# Revit family: Урна уличная круглая «Парко» Арт 12916
name_source: partatom
category: Антураж
revit_build: Autodesk Revit 2018 (Build: 20180423_1000(x64)
units: mm (PartAtom-declared; Revit-internal decimal feet)

## family parameters
Всегда вертикально = Да
Источник визуального образа = Геометрия семейства
На основе рабочей плоскости = Нет
Общий = Нет
При загрузке вырезать с полостями = Нет
Точка расчета площади = Нет

## types (2) — shared parameters
URL = https://hobbyka.ru
Артикул товара = Арт. 12916
Высота = 600 мм
Группа модели = Уличные урны
Диаметр = 388 мм
Длина = 388 мм
Изготовитель = ООО «Хоббика»
Изображение типоразмера = Урна уличная круглая «Парко» Арт 12916.jpg
Материал изделия = Сталь
Ширина = 388 мм

## per-type parameters (varying)
| type | Нержавеющая сталь | Описание | Сталь | Цвет урны |
| Версия "Сталь" | Нет | Урна уличная круглая «Парко». Версия сталь | Да | Сталь |
| Версия "Нержавеющая сталь" | Да | Урна уличная круглая «Парко». Версия нержавеющая сталь | Нет | Нержавеющая сталь |
